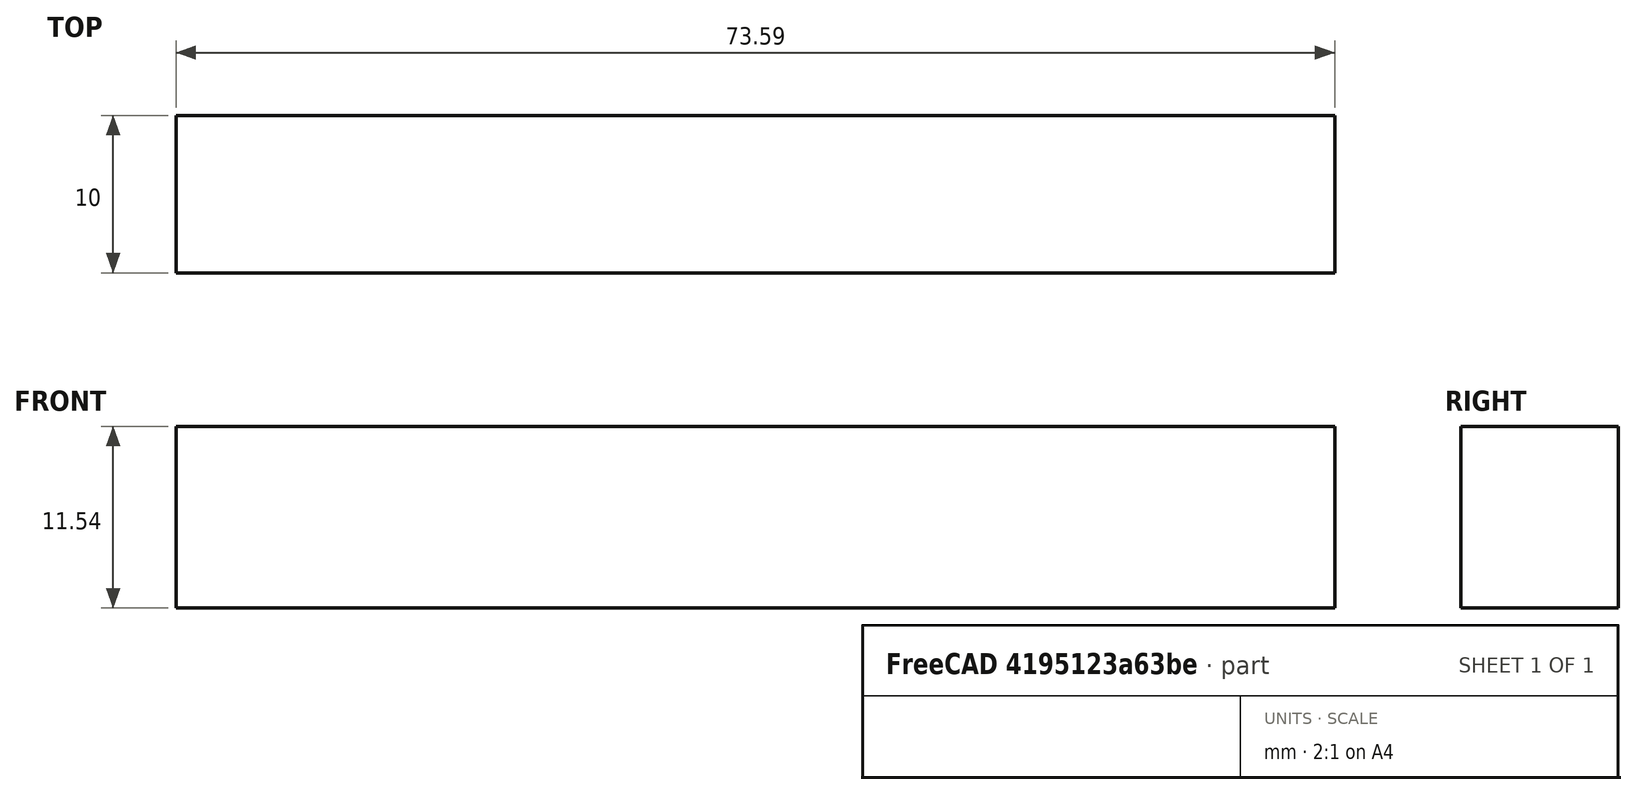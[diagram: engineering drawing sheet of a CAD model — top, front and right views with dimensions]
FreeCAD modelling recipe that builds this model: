
FCSTD DOCUMENT  (FreeCAD 1.0R38806 (Git))
Label: ExtrusionPorTrayectoria
License: All rights reserved
LicenseURL: http://en.wikipedia.org/wiki/All_rights_reserved
objects: Sketcher::SketchObject×2, PartDesign::Body×1, Part::Sweep×1
note: 6 computed .brp shape members not serialized (recipe doc carries the construction recipe); baked Part::Feature solids carry a one-line shape summary decoded from their .brp

FEATURE [Sketcher::SketchObject] Sketch
  ArcFitTolerance = 1e-06
  AttachmentSupport = -> [YZ_Plane]
  FullyConstrained = false
  MakeInternals = false
  MapMode = 5
  Placement = pos=(0,0,0) rot=(0.57735,0.57735,0.57735;2.0944rad)
  sketch-geometry (4):
    g0: LineSegment StartX=-5.00016 StartY=5.7692 StartZ=0 EndX=-5.00016 EndY=-5.7692 EndZ=0
    g1: LineSegment StartX=-5.00016 StartY=-5.7692 StartZ=0 EndX=5.00016 EndY=-5.7692 EndZ=0
    g2: LineSegment StartX=5.00016 StartY=-5.7692 StartZ=0 EndX=5.00016 EndY=5.7692 EndZ=0
    g3: LineSegment StartX=5.00016 StartY=5.7692 StartZ=0 EndX=-5.00016 EndY=5.7692 EndZ=0
  constraints (8):
    c: Coincident(g0,g1)
    c: Coincident(g1,g2)
    c: Coincident(g2,g3)
    c: Coincident(g3,g0)
    c: Vertical(g2)
    c: Horizontal(g1)
    c: Symmetric(g2,g0,g-2)
    c: Symmetric(g0,g0,g-1)
FEATURE [Sketcher::SketchObject] Sketch001
  ArcFitTolerance = 1e-06
  AttachmentSupport = -> [XZ_Plane]
  FullyConstrained = false
  MakeInternals = false
  MapMode = 5
  Placement = pos=(0,0,0) rot=(1,0,0;1.5708rad)
  sketch-geometry (1):
    g0: LineSegment StartX=0 StartY=0 StartZ=0 EndX=73.5897 EndY=0 EndZ=0
  constraints (2):
    c: Coincident(g0,g-1)
    c: Horizontal(g0)
FEATURE [PartDesign::Body] Body
  AllowCompound = false
  Group = -> [Sketch,Sketch001]
  Origin = -> Origin
FEATURE [Part::Sweep] Sweep
  Frenet = true
  Sections = -> [Sketch]
  Solid = false
  Spine = -> Sketch001 [Edge1]
  Transition = 1
